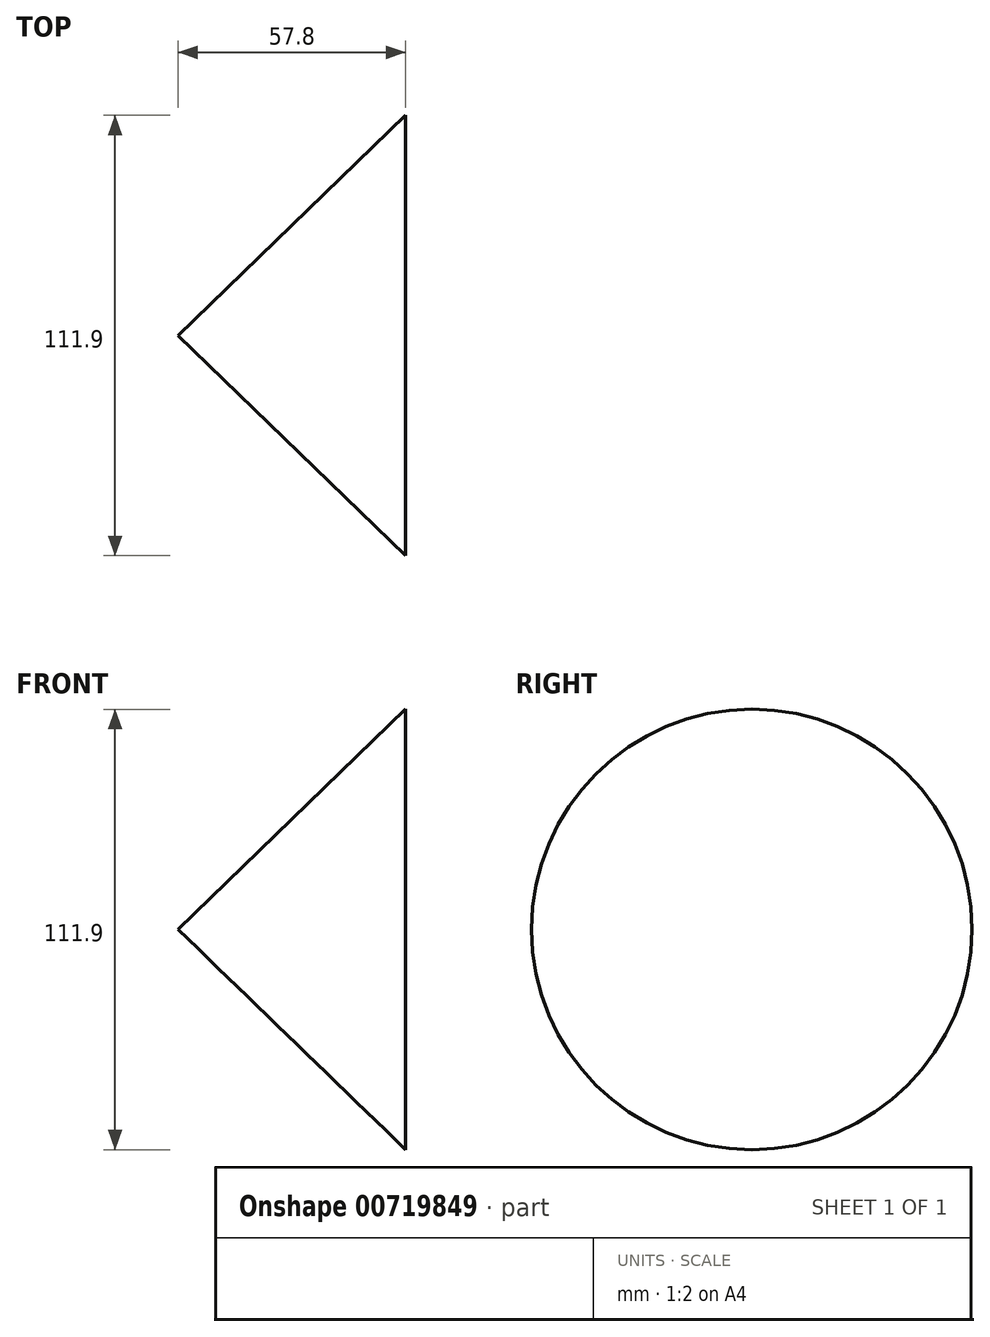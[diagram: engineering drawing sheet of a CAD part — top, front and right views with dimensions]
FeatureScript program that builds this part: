
annotation { "Feature Type Name" : "Feature", "Feature Type Description" : "" }
export const myFeature = defineFeature(function(context is Context, id is Id, definition is map)
    precondition{}
    {
        {
            var Q0;
            Q0=qCreatedBy(makeId("Front.planeOp"),FACE);
            var sketch = newSketch(context, id + "F0", { "sketchPlane" : qUnion([Q0])});
            skLineSegment(sketch, "E0", {"start": v(0, 55.95) * mm, "end": v(-57.8, 0) * mm});
            skLineSegment(sketch, "E1", {"start": v(-57.8, 0) * mm, "end": v(0, 0) * mm});
            skSolve(sketch);
        }
        {
            var Q0;
            Q0=sQuery(id+"F0.wireOp",EDGE,"E0");
            var Q1;
            Q1=sQuery(id+"F0.wireOp",EDGE,"E1");
            revolve(context, id + "F1", {"bodyType" : ToolBodyType.SURFACE, "surfaceOperationType" : NewSurfaceOperationType.NEW, "surfaceEntities" : qUnion([Q0]), "axis" : qUnion([Q1]), "revolveType" : RevolveType.FULL});
        }
    });
